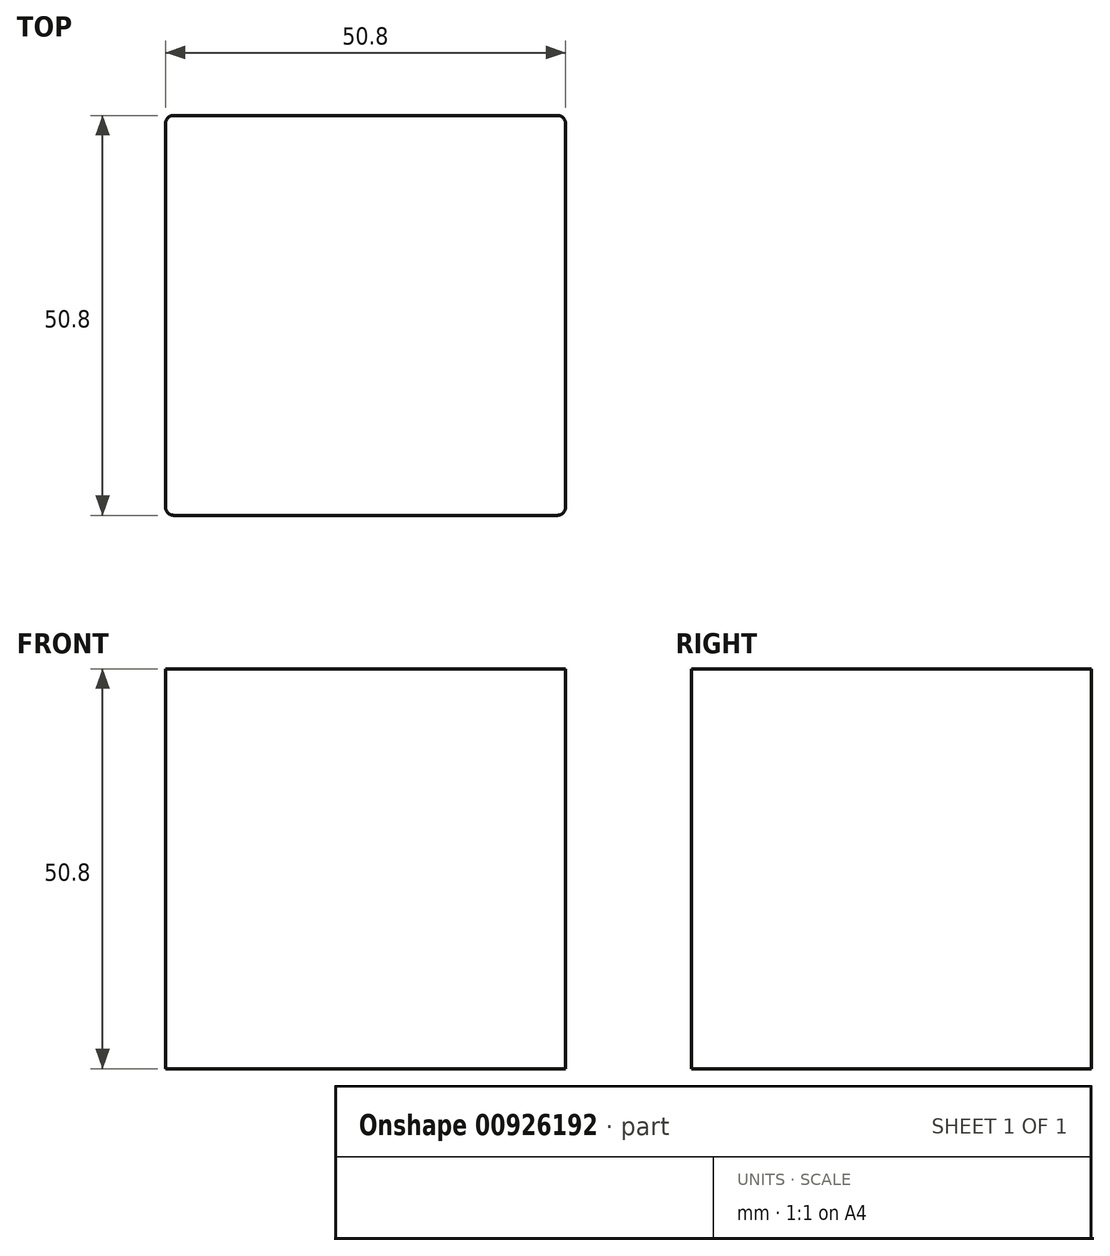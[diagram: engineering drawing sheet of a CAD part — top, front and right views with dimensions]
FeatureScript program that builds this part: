
annotation { "Feature Type Name" : "Feature", "Feature Type Description" : "" }
export const myFeature = defineFeature(function(context is Context, id is Id, definition is map)
    precondition{}
    {
        {
            var Q0;
            Q0=qCreatedBy(makeId("Front.planeOp"),FACE);
            var sketch = newSketch(context, id + "F0", { "sketchPlane" : qUnion([Q0])});
            skLineSegment(sketch, "E0.bottom", {"start": v(25.4, 25.4) * mm, "end": v(-25.4, 25.4) * mm});
            skLineSegment(sketch, "E0.top", {"start": v(25.4, -25.4) * mm, "end": v(-25.4, -25.4) * mm});
            skLineSegment(sketch, "E0.left", {"start": v(25.4, 25.4) * mm, "end": v(25.4, -25.4) * mm});
            skLineSegment(sketch, "E0.right", {"start": v(-25.4, 25.4) * mm, "end": v(-25.4, -25.4) * mm});
            skPoint(sketch, "E0.middle", {"position": v(0, 0) * mm});
            skSolve(sketch);
        }
        {
            var Q0;
            Q0 = qSketchRegion(id + "F0", true);
            extrude(context, id + "F1", {"entities" : qUnion([Q0]), "depth" : 25.4 * mm, "offsetDistance" : 25.4 * mm});
        }
        {
            var Q0;
            Q0=makeQuery(id+"F1.opExtrude","CAP_FACE",FACE,{"disambiguationData":[OSD([sQuery(id+"F0.wireOp",EDGE,"E0.bottom"),sQuery(id+"F0.wireOp",EDGE,"E0.top"),sQuery(id+"F0.wireOp",EDGE,"E0.left"),sQuery(id+"F0.wireOp",EDGE,"E0.right")])],"isStart":true});
            extrude(context, id + "F2", {"entities" : qUnion([Q0]), "operationType" : NewBodyOperationType.ADD, "depth" : 25.4 * mm, "offsetDistance" : 25.4 * mm});
        }
        {
            var Q0;
            Q0=makeQuery(id+"F1.opExtrude","CAP_EDGE",EDGE,{"disambiguationData":[OSD([sQuery(id+"F0.wireOp",EDGE,"E0.left")])],"isStart":false});
            var Q1;
            Q1=makeQuery(id+"F2.opExtrude","CAP_EDGE",EDGE,{"disambiguationData":[OSD([sQuery(id+"F0.wireOp",EDGE,"E0.left")])],"isStart":false});
            var Q2;
            Q2=makeQuery(id+"F2.opExtrude","CAP_EDGE",EDGE,{"disambiguationData":[OSD([sQuery(id+"F0.wireOp",EDGE,"E0.right")])],"isStart":false});
            var Q3;
            Q3=makeQuery(id+"F1.opExtrude","CAP_EDGE",EDGE,{"disambiguationData":[OSD([sQuery(id+"F0.wireOp",EDGE,"E0.right")])],"isStart":false});
            fillet(context, id + "F3", {"entities" : qUnion([Q0, Q1, Q2, Q3]), "radius" : 1.02 * mm, "tangentPropagation" : true, "allowEdgeOverflow" : false});
        }
    });
